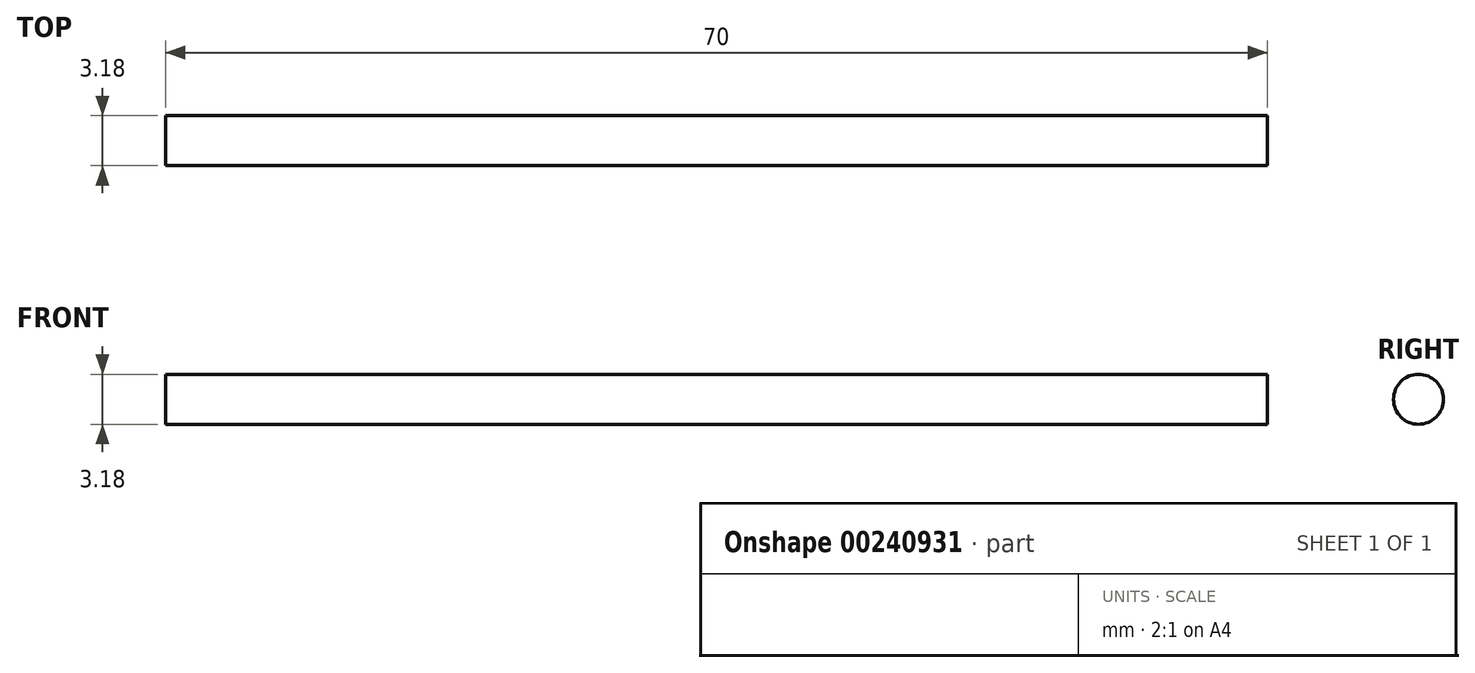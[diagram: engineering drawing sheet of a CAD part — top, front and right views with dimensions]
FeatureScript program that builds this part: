
annotation { "Feature Type Name" : "Feature", "Feature Type Description" : "" }
export const myFeature = defineFeature(function(context is Context, id is Id, definition is map)
    precondition{}
    {
        {
            var Q0;
            Q0=qCreatedBy(makeId("Right.planeOp"),FACE);
            var sketch = newSketch(context, id + "F0", { "sketchPlane" : qUnion([Q0])});
            skCircle(sketch, "E0", {"center": v(0, 0) * mm, "radius": 1.6 * mm});
            skSolve(sketch);
        }
        {
            var Q0;
            Q0 = qSketchRegion(id + "F0", true);
            extrude(context, id + "F1", {"entities" : qUnion([Q0]), "depth" : 70 * mm});
        }
    });
